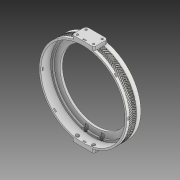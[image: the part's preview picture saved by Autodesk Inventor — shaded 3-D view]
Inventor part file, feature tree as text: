
AUTODESK INVENTOR PART (.ipt)
format: ipt  version: 2020 (Build 240168000, 168)  size: 2,975,232 bytes
history: native  units: in
note: dims shown in document units (in); Inventor stores cm internally (conversion verified against a paired STEP export)
features: other x5, extrude x5, sketch x5, plane x3, fillet x2, mirror x1
ambient origin geometry x8: Origin, YZ Plane, XZ Plane, XY Plane, X Axis, Y Axis, Z Axis, Center Point
bodies: Solid2 (feature_tree), Solid1 (feature_tree)
feature tree (21):
  other  "Blocks"
  extrude  "Extrusion1"  Depth=0.3937in
  extrude  "Extrusion3"  Depth=3.1496in
  plane  "Work Plane1"
  extrude  "Extrusion4"  Depth=0.4724in
  extrude  "Extrusion5"  Depth=1.1024in
  plane  "Work Plane2"
  extrude  "Extrusion6"  Depth=0.1181in TaperAngle=0.0deg
  fillet  "Fillet1"  [1 undecoded]
  mirror  "Mirror1"
  fillet  "Fillet2"  Radius=0.2362in
  sketch  "Sketch1"  dims[d0=0.0in d1=0.0in d5=0.3937in]
  sketch  "Sketch3"  dims[d6=0.1575in d7=0.0in d8=3.1496in]
  sketch  "Sketch4"  dims[d9=0.1575in d10=0.0in d11=0.4724in]
  other  "Block1"
  other  "Block2"
  sketch  "Sketch5"  dims[d12=0.5906in d13=1.1024in]
  sketch  "Sketch6"  dims[d14=0.1378in d15=0.6299in d16=0.0in d17=-0.1969in d18=0.2362in d19=0.3937in d20=0.0in d21=0.0787in d22=0.1181in]
  plane  "Work Plane3"
  other  "Block2:1"
  other  "Block1:2"
note: 1 required parameter value undecoded (feature->parameter linkage not recoverable at this tier; creation-order binding heuristic only, values carry confidence <= 0.55)
